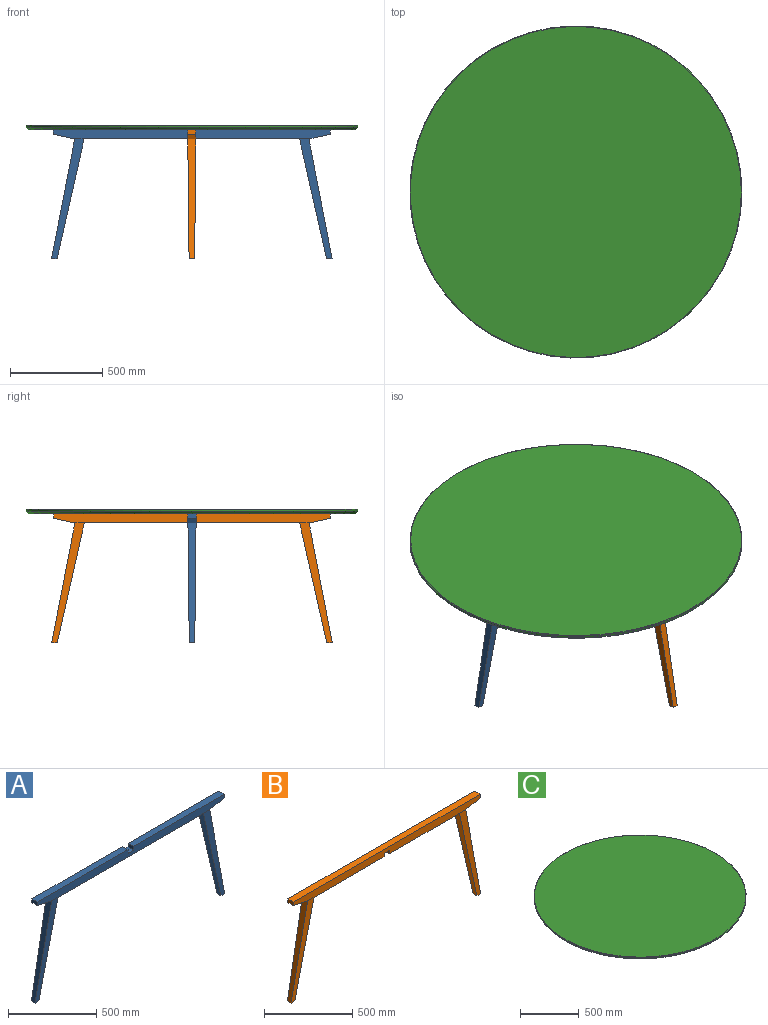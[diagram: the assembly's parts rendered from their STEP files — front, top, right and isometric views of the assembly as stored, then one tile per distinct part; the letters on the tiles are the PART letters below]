
ASSEMBLY  parts=3 mates=2
PART A: 22 faces, bbox 1520x44x700 mm
  f0: plane 30x30mm, normal (0,0,-1), area 900mm2, adj f2,f3,f20,f21
  f1: plane 30x30mm, normal (0,0,-1), area 900mm2, adj f4,f5,f18,f19
  f2: plane 650x146.28mm, normal (-0.98,0,-0.22), area 24651.5mm2, adj f0,f8,f20,f21
  f3: plane 650x125.36mm, normal (0.98,0,0.19), area 24493.2mm2, adj f0,f9,f20,f21
  f4: plane 650x125.36mm, normal (-0.98,0,0.19), area 24493.2mm2, adj f1,f17,f18,f19
  f5: plane 650x146.28mm, normal (0.98,0,-0.22), area 24651.5mm2, adj f1,f8,f18,f19
  f6: plane 1500x50mm, normal (0,-1,0), area 71016.1mm2, adj f8,f9,f10,f11,f12,f13,f14,f15
  f7: plane 1500x50mm, normal (0,1,0), area 71016.1mm2, adj f8,f9,f10,f11,f12,f13,f14,f15
  f8: plane 1167.44x44mm, normal (0,0,-1), area 51367.5mm2, adj f2,f5,f6,f7
  f9: plane 115.36x44mm, normal (0.21,0,-0.98), area 5193.5mm2, adj f3,f6,f7,f10
  f10: plane 44x25mm, normal (1,0,0), area 1100mm2, adj f6,f7,f9,f11
  f11: plane 728x44mm, normal (0,0,1), area 32032mm2, adj f6,f7,f10,f12
  f12: plane 44x25mm, normal (-1,0,0), area 1100mm2, adj f6,f7,f11,f13
  f13: plane 44x44mm, normal (0,0,1), area 1936mm2, adj f6,f7,f12,f14
  f14: plane 44x25mm, normal (1,0,0), area 1100mm2, adj f6,f7,f13,f15
  f15: plane 728x44mm, normal (0,0,1), area 32032mm2, adj f6,f7,f14,f16
  f16: plane 44x25mm, normal (-1,0,0), area 1100mm2, adj f6,f7,f15,f17
  f17: plane 115.36x44mm, normal (-0.21,0,-0.98), area 5193.5mm2, adj f4,f6,f7,f16
  f18: plane 650x176.28mm, normal (0,-1,-0.01), area 26301mm2, adj f1,f4,f5,f6
  f19: plane 650x176.28mm, normal (0,1,-0.01), area 26301mm2, adj f1,f4,f5,f7
  f20: plane 650x176.28mm, normal (0,-1,-0.01), area 26301mm2, adj f0,f2,f3,f6
  f21: plane 650x176.28mm, normal (0,1,-0.01), area 26301mm2, adj f0,f2,f3,f7
PART B: 22 faces, bbox 1520x44x700 mm
  f0: plane 30x30mm, normal (0,0,-1), area 900mm2, adj f2,f3,f20,f21
  f1: plane 30x30mm, normal (0,0,-1), area 900mm2, adj f4,f5,f18,f19
  f2: plane 650x125.36mm, normal (-0.98,0,0.19), area 24493.2mm2, adj f0,f10,f20,f21
  f3: plane 650x146.28mm, normal (0.98,0,-0.22), area 24651.5mm2, adj f0,f11,f20,f21
  f4: plane 650x146.28mm, normal (-0.98,0,-0.22), area 24651.5mm2, adj f1,f15,f18,f19
  f5: plane 650x125.36mm, normal (0.98,0,0.19), area 24493.2mm2, adj f1,f16,f18,f19
  f6: plane 1500x50mm, normal (0,-1,0), area 71016.1mm2, adj f8,f9,f10,f11,f12,f13,f14,f15
  f7: plane 1500x50mm, normal (0,1,0), area 71016.1mm2, adj f8,f9,f10,f11,f12,f13,f14,f15
  f8: plane 1500x44mm, normal (0,0,1), area 66000mm2, adj f6,f7,f9,f17
  f9: plane 44x25mm, normal (-1,0,0), area 1100mm2, adj f6,f7,f8,f10
  f10: plane 115.36x44mm, normal (-0.21,0,-0.98), area 5193.5mm2, adj f2,f6,f7,f9
  f11: plane 561.72x44mm, normal (0,0,-1), area 24715.7mm2, adj f3,f6,f7,f12
  f12: plane 44x25mm, normal (1,0,0), area 1100mm2, adj f6,f7,f11,f13
  f13: plane 44x44mm, normal (0,0,-1), area 1936mm2, adj f6,f7,f12,f14
  f14: plane 44x25mm, normal (-1,0,0), area 1100mm2, adj f6,f7,f13,f15
  f15: plane 561.72x44mm, normal (0,0,-1), area 24715.7mm2, adj f4,f6,f7,f14
  f16: plane 115.36x44mm, normal (0.21,0,-0.98), area 5193.5mm2, adj f5,f6,f7,f17
  f17: plane 44x25mm, normal (1,0,0), area 1100mm2, adj f6,f7,f8,f16
  f18: plane 650x176.28mm, normal (0,-1,-0.01), area 26301mm2, adj f1,f4,f5,f6
  f19: plane 650x176.28mm, normal (0,1,-0.01), area 26301mm2, adj f1,f4,f5,f7
  f20: plane 650x176.28mm, normal (0,-1,-0.01), area 26301mm2, adj f0,f2,f3,f6
  f21: plane 650x176.28mm, normal (0,1,-0.01), area 26301mm2, adj f0,f2,f3,f7
PART C: 5 faces, bbox 1948.3x1948.3x25 mm
  f0: cylinder r=900mm len=1800mm, axis (0,0,-1), area 53721.2mm2, adj f3,f4
  f1: plane 1794x1794mm, normal (0,0,1), area 2527753.7mm2, adj f4
  f2: plane 1775x1775mm, normal (0,0,-1), area 2474495.1mm2, adj f3
  f3: cone r=900mm half-angle=45deg, axis (0,0,1), area 99270.7mm2, adj f0,f2
  f4: torus R=897mm, axis (0,0,1), area 26615.7mm2, adj f0,f1
PLACE A t=(149.69,408.31,-430.25)mm
PLACE B rot(axis=(0,0,-1),90deg) t=(171.69,386.31,-430.25)mm
PLACE C t=(149.69,386.31,-430.25)mm
MATE parallel C.f0 <-> B.f8  axis (0,0,-1) through (149.69,386.31,-430.25)mm
MATE parallel B.f13 <-> A.f13  axis (0,0,-1) through (149.69,386.31,-455.25)mm
